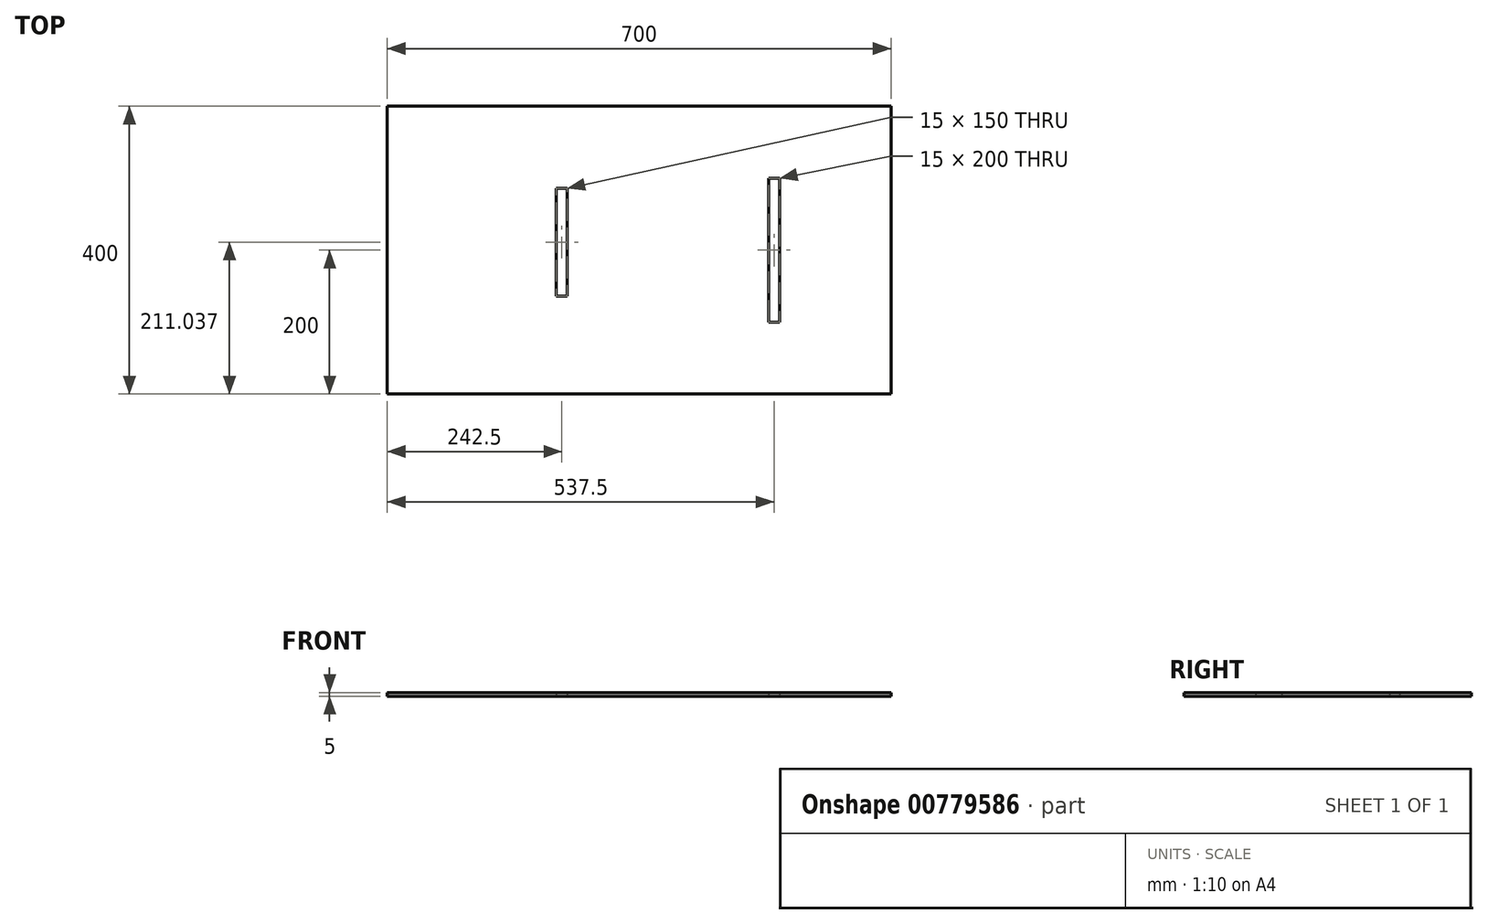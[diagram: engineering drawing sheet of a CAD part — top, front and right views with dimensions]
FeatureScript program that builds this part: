
annotation { "Feature Type Name" : "Feature", "Feature Type Description" : "" }
export const myFeature = defineFeature(function(context is Context, id is Id, definition is map)
    precondition{}
    {
        {
            var Q0;
            Q0=qCreatedBy(makeId("Top.planeOp"),FACE);
            var sketch = newSketch(context, id + "F0", { "sketchPlane" : qUnion([Q0])});
            skLineSegment(sketch, "E0.bottom", {"start": v(350, 200) * mm, "end": v(-350, 200) * mm});
            skLineSegment(sketch, "E0.top", {"start": v(350, -200) * mm, "end": v(-350, -200) * mm});
            skLineSegment(sketch, "E0.left", {"start": v(350, 200) * mm, "end": v(350, -200) * mm});
            skLineSegment(sketch, "E0.right", {"start": v(-350, 200) * mm, "end": v(-350, -200) * mm});
            skPoint(sketch, "E0.middle", {"position": v(0, 0) * mm});
            skSolve(sketch);
        }
        {
            var Q0;
            Q0 = qSketchRegion(id + "F0", true);
            extrude(context, id + "F1", {"entities" : qUnion([Q0]), "depth" : 5 * mm, "offsetDistance" : 25 * mm});
        }
        {
            var Q0;
            Q0=makeQuery(id+"F1.opExtrude","CAP_FACE",FACE,{"disambiguationData":[OSD([sQuery(id+"F0.wireOp",EDGE,"E0.bottom"),sQuery(id+"F0.wireOp",EDGE,"E0.top"),sQuery(id+"F0.wireOp",EDGE,"E0.left"),sQuery(id+"F0.wireOp",EDGE,"E0.right")])],"isStart":true});
            var sketch = newSketch(context, id + "F2", { "sketchPlane" : qUnion([Q0])});
            skLineSegment(sketch, "E1.bottom", {"start": v(195, -100) * mm, "end": v(180, -100) * mm});
            skLineSegment(sketch, "E1.top", {"start": v(195, 100) * mm, "end": v(180, 100) * mm});
            skLineSegment(sketch, "E1.left", {"start": v(195, -100) * mm, "end": v(195, 100) * mm});
            skLineSegment(sketch, "E1.right", {"start": v(180, -100) * mm, "end": v(180, 100) * mm});
            skLineSegment(sketch, "E2.bottom", {"start": v(-100, -86.04) * mm, "end": v(-115, -86.04) * mm});
            skLineSegment(sketch, "E2.top", {"start": v(-100, 63.96) * mm, "end": v(-115, 63.96) * mm});
            skLineSegment(sketch, "E2.left", {"start": v(-100, -86.04) * mm, "end": v(-100, 63.96) * mm});
            skLineSegment(sketch, "E2.right", {"start": v(-115, -86.04) * mm, "end": v(-115, 63.96) * mm});
            skSolve(sketch);
        }
        {
            var Q0;
            Q0 = qSketchRegion(id + "F2", true);
            extrude(context, id + "F3", {"entities" : qUnion([Q0]), "operationType" : NewBodyOperationType.REMOVE, "oppositeDirection" : true, "depth" : 25 * mm, "offsetDistance" : 25 * mm});
        }
    });
